# Revit family: VR2-2207-LHT_v1.2015.02.01_detailed
name_source: partatom
category: Mechanical Equipment
revit_build: Autodesk Revit Architecture 2012 (Build: 20110309_2315(x64)
units: mm (PartAtom-declared; Revit-internal decimal feet)

## types (1)
- VR2-2207-LHT_v1.2015.02.01_detailed
    Description = Dutypoint Systems WRAS-approved variable speed compact cold water booster set fitted with 2 multistage vertical pumps (AISI 304 stainless steel casings) with motor-mounted variable speed drives, 4 isolation valves (EN12165 Cu Zn 40), 2 single disc non-return valves (AISI 304/316) and 2 pressure vessels (certified to PED 97/23/C). Mounted on a powder coated mild steel base assembly with integral anti-vibration mounts.  All fasteners are to BS EN3506 A2.70/BS3643. The control panel features a door-interlocked isolator, individual pump isolators, power on and fault lamps. A common fault volt-free contact and low-water connection device contacts are included as standard. The footprint of the set completely contains the pumps, pressure vessels, manifolds, valves and control panel.
    Dry Weight = 263kg
    FLC (per Pump) = 14.5A
    FLC Total (all pumps) = 29A
    Inlet Size = DN80
    Manufacturer = Dutypoint Systems
    Manufacturers Website = http://www.dutypoint.com
    Max Flow = 58m³/hr
    Max Head = 108.5m
    Model = VR2-2207-LHT
    Motor Size = 7.5kW
    Outlet Size = DN80
    Performance Curve = http://www.dutypoint.com
    Supply Voltage = 400/3/50
    Version = v1.2015.02.01
    Version Date = 01.02.2015
    WRAS Approval = Yes
    WRAS Approval No. = 1310317

## geometry (parser evidence)
native form markers: Blend x12, Sweep x101
no freeform markers — native parametric forms only
